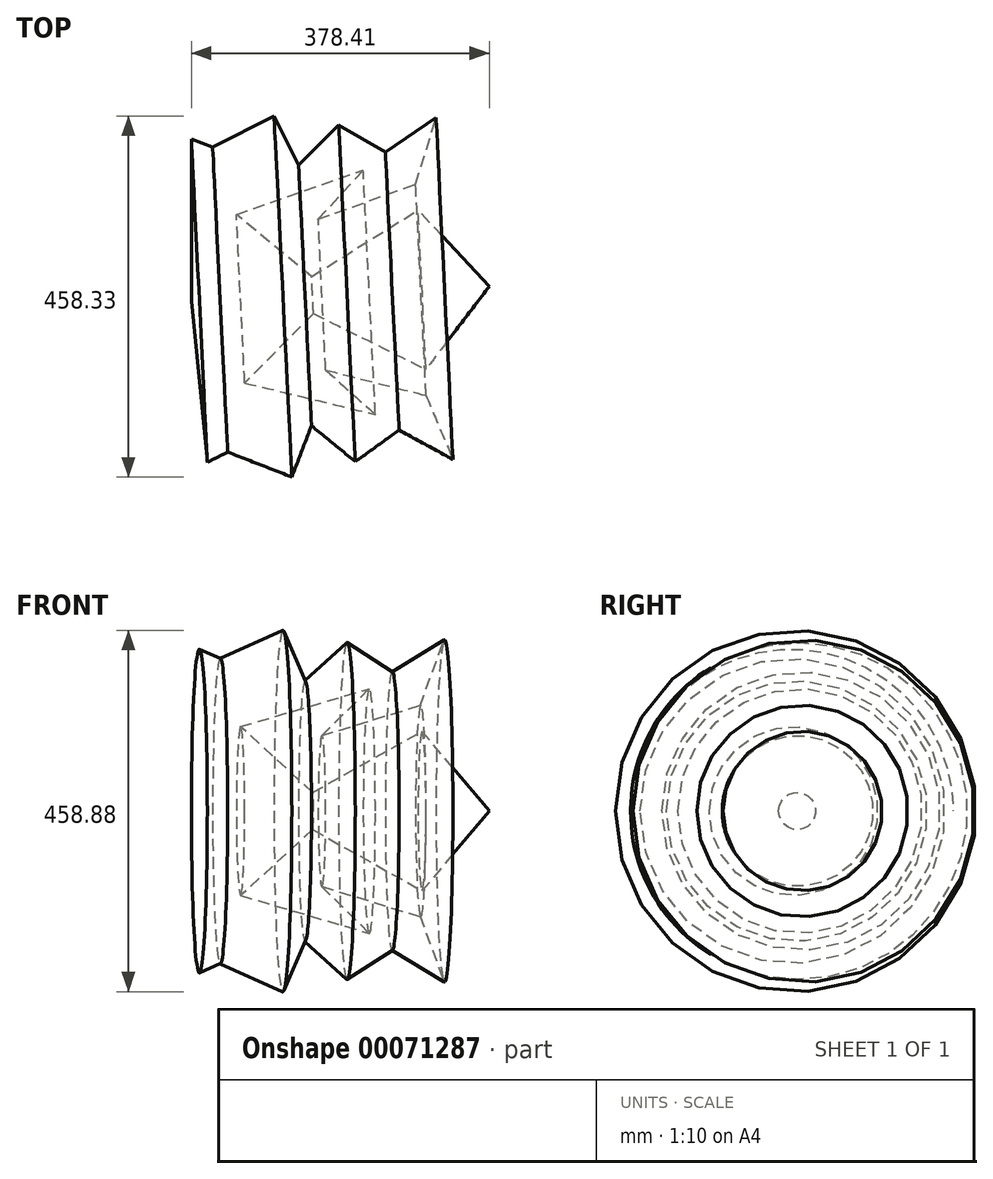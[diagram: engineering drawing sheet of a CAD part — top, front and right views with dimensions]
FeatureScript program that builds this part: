
annotation { "Feature Type Name" : "Feature", "Feature Type Description" : "" }
export const myFeature = defineFeature(function(context is Context, id is Id, definition is map)
    precondition{}
    {
        {
            var Q0;
            Q0=qCreatedBy(makeId("Top.planeOp"),FACE);
            var sketch = newSketch(context, id + "F0", { "sketchPlane" : qUnion([Q0])});
            skLineSegment(sketch, "E0", {"start": v(-205.47, 90.19) * mm, "end": v(-205.47, -115.65) * mm});
            skLineSegment(sketch, "E1", {"start": v(-206.51, -115.65) * mm, "end": v(172.94, -96.94) * mm});
            skLineSegment(sketch, "E2", {"start": v(172.94, -96.94) * mm, "end": v(82.5, 0) * mm});
            skLineSegment(sketch, "E3", {"start": v(82.5, 0) * mm, "end": v(-52.65, -84.46) * mm});
            skLineSegment(sketch, "E4", {"start": v(-52.65, -84.46) * mm, "end": v(-148.3, -5.45) * mm});
            skLineSegment(sketch, "E5", {"start": v(-148.3, -5.45) * mm, "end": v(12.84, 50.68) * mm});
            skLineSegment(sketch, "E6", {"start": v(12.84, 50.68) * mm, "end": v(-44.33, -11.7) * mm});
            skLineSegment(sketch, "E7", {"start": v(-44.33, -11.7) * mm, "end": v(79.38, 33.01) * mm});
            skLineSegment(sketch, "E8", {"start": v(79.38, 33.01) * mm, "end": v(105.37, 117.22) * mm});
            skLineSegment(sketch, "E9", {"start": v(105.37, 117.22) * mm, "end": v(40.91, 73.56) * mm});
            skLineSegment(sketch, "E10", {"start": v(40.91, 73.56) * mm, "end": v(-18.34, 107.86) * mm});
            skLineSegment(sketch, "E11", {"start": v(-18.34, 107.86) * mm, "end": v(-69.29, 56.92) * mm});
            skLineSegment(sketch, "E12", {"start": v(-69.29, 56.92) * mm, "end": v(-100.47, 119.3) * mm});
            skLineSegment(sketch, "E13", {"start": v(-100.47, 119.3) * mm, "end": v(-178.44, 79.8) * mm});
            skLineSegment(sketch, "E14", {"start": v(-178.44, 79.8) * mm, "end": v(-205.47, 90.19) * mm});
            skSolve(sketch);
        }
        {
            var Q0;
            {var subQ4=sQuery(id+"F0.wireOp",EDGE,"E2");Q0=makeQuery(id+"F0.imprint","IMPRINT",FACE,{"disambiguationData":[TD([[makeQuery(id+"F0.imprint","IMPRINT",EDGE,{"derivedFrom":subQ4}),1.0]])]});}
            var Q1;
            Q1=sQuery(id+"F0.wireOp",EDGE,"E1");
            revolve(context, id + "F1", {"entities" : qUnion([Q0]), "axis" : qUnion([Q1]), "revolveType" : RevolveType.FULL});
        }
    });
